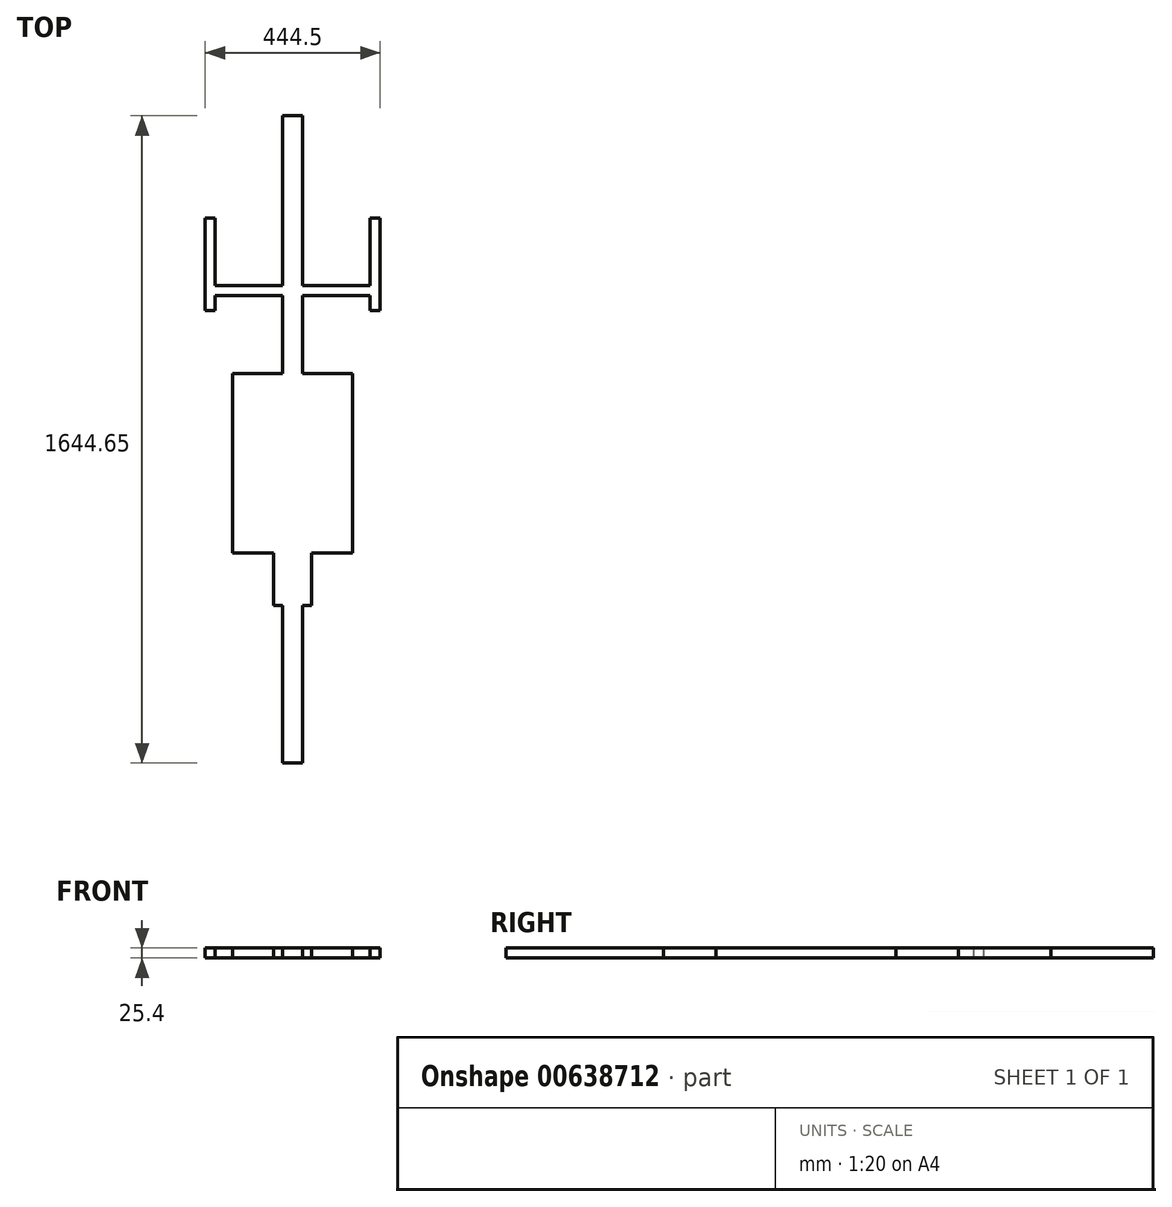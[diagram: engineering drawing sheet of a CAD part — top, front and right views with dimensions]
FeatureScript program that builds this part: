
annotation { "Feature Type Name" : "Feature", "Feature Type Description" : "" }
export const myFeature = defineFeature(function(context is Context, id is Id, definition is map)
    precondition{}
    {
        {
            var Q0;
            Q0=qCreatedBy(makeId("Top.planeOp"),FACE);
            var sketch = newSketch(context, id + "F0", { "sketchPlane" : qUnion([Q0])});
            skLineSegment(sketch, "E0.bottom", {"start": v(-25.4, 0) * mm, "end": v(25.4, 0) * mm});
            skLineSegment(sketch, "E0.top", {"start": v(-25.4, 1644.65) * mm, "end": v(25.4, 1644.65) * mm});
            skLineSegment(sketch, "E0.left", {"start": v(-25.4, 0) * mm, "end": v(-25.4, 1644.65) * mm});
            skLineSegment(sketch, "E0.right", {"start": v(25.4, 0) * mm, "end": v(25.4, 1644.65) * mm});
            skLineSegment(sketch, "E1.bottom", {"start": v(48.57, 400.05) * mm, "end": v(-48.57, 400.05) * mm});
            skLineSegment(sketch, "E1.top", {"start": v(48.57, 621.77) * mm, "end": v(-48.57, 621.77) * mm});
            skLineSegment(sketch, "E1.left", {"start": v(48.57, 400.05) * mm, "end": v(48.57, 621.77) * mm});
            skLineSegment(sketch, "E1.right", {"start": v(-48.57, 400.05) * mm, "end": v(-48.57, 621.77) * mm});
            skPoint(sketch, "E1.middle", {"position": v(0, 510.91) * mm});
            skLineSegment(sketch, "E2.bottom", {"start": v(196.85, 1187.45) * mm, "end": v(-196.85, 1187.45) * mm});
            skLineSegment(sketch, "E2.top", {"start": v(222.25, 1384.3) * mm, "end": v(196.85, 1384.3) * mm});
            skLineSegment(sketch, "E2.left", {"start": v(222.25, 1149.35) * mm, "end": v(222.25, 1384.3) * mm});
            skLineSegment(sketch, "E2.right", {"start": v(-222.25, 1149.35) * mm, "end": v(-222.25, 1384.3) * mm});
            skPoint(sketch, "E2.middle", {"position": v(0, 1379.56) * mm});
            skLineSegment(sketch, "E3.bottom", {"start": v(152.4, 533.4) * mm, "end": v(-152.4, 533.4) * mm});
            skLineSegment(sketch, "E3.top", {"start": v(152.4, 990.15) * mm, "end": v(-152.4, 990.15) * mm});
            skLineSegment(sketch, "E3.left", {"start": v(152.4, 533.4) * mm, "end": v(152.4, 990.15) * mm});
            skLineSegment(sketch, "E3.right", {"start": v(-152.4, 533.4) * mm, "end": v(-152.4, 990.15) * mm});
            skPoint(sketch, "E3.middle", {"position": v(0, 761.77) * mm});
            skLineSegment(sketch, "E4.bottom", {"start": v(196.85, 1212.85) * mm, "end": v(-196.85, 1212.85) * mm});
            skLineSegment(sketch, "E4.left", {"start": v(196.85, 1149.35) * mm, "end": v(196.85, 1187.45) * mm});
            skLineSegment(sketch, "E4.right", {"start": v(-196.85, 1212.85) * mm, "end": v(-196.85, 1384.3) * mm});
            skLineSegment(sketch, "E5.trimOffspring", {"start": v(-196.85, 1384.3) * mm, "end": v(-222.25, 1384.3) * mm});
            skLineSegment(sketch, "E6", {"start": v(-196.85, 1187.45) * mm, "end": v(-196.85, 1149.35) * mm});
            skLineSegment(sketch, "E7", {"start": v(-196.85, 1149.35) * mm, "end": v(-222.25, 1149.35) * mm});
            skLineSegment(sketch, "E8", {"start": v(222.25, 1149.35) * mm, "end": v(196.85, 1149.35) * mm});
            skLineSegment(sketch, "E9.trimOffspring", {"start": v(196.85, 1212.85) * mm, "end": v(196.85, 1384.3) * mm});
            skSolve(sketch);
        }
        {
            var Q0;
            Q0=qSketchRegion(id+"F0",true);
            var Q1;
            {var subQ0=sQuery(id+"F0.wireOp",EDGE,"E3.bottom");var subQ1=sQuery(id+"F0.wireOp",EDGE,"E0.left");var subQ2=makeQuery(id+"F0.imprint","INTERSECT",VERTEX,{"derivedFrom":[subQ1,subQ0]});Q1=makeQuery(id+"F0.imprint","IMPRINT",FACE,{"disambiguationData":[TD([[makeQuery(id+"F0.imprint","IMPRINT",EDGE,{"disambiguationData":[TD([[subQ2,-1.0]])],"derivedFrom":subQ1}),-1.0]])]});}
            extrude(context, id + "F1", {"entities" : qUnion([Q0, Q1]), "depth" : 25.4 * mm, "offsetDistance" : 25.4 * mm});
        }
    });
